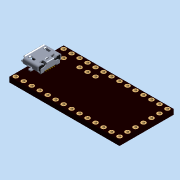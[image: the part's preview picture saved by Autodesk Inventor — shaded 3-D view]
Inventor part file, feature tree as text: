
AUTODESK INVENTOR PART (.ipt)
format: ipt  version: 2015 (Build 190159000, 159)  size: 808,960 bytes
history: native  units: mm (DEFAULTED — no unit token found)
features: hole x37, other x3
ambient origin geometry x8: Origin, YZ Plane, XZ Plane, XY Plane, X Axis, Y Axis, Z Axis, Center Point
bodies: Solid1 (feature_tree)
feature tree (40):
  other  "Teensy 3.1.iam"
  other  "Teensy 3.1 PCB.ipt:1"
  other  "micro_usb_47346-0001.ipt:1"
  hole  "Hole metalization.ipt:1"  [1 undecoded]
  hole  "Hole metalization.ipt:2"  [1 undecoded]
  hole  "Hole metalization.ipt:3"  [1 undecoded]
  hole  "Hole metalization.ipt:4"  [1 undecoded]
  hole  "Hole metalization.ipt:5"  [1 undecoded]
  hole  "Hole metalization.ipt:6"  [1 undecoded]
  hole  "Hole metalization.ipt:7"  [1 undecoded]
  hole  "Hole metalization.ipt:8"  [1 undecoded]
  hole  "Hole metalization.ipt:9"  [1 undecoded]
  hole  "Hole metalization.ipt:10"  [1 undecoded]
  hole  "Hole metalization.ipt:11"  [1 undecoded]
  hole  "Hole metalization.ipt:12"  [1 undecoded]
  hole  "Hole metalization.ipt:13"  [1 undecoded]
  hole  "Hole metalization.ipt:14"  [1 undecoded]
  hole  "Hole metalization.ipt:15"  [1 undecoded]
  hole  "Hole metalization.ipt:16"  [1 undecoded]
  hole  "Hole metalization.ipt:17"  [1 undecoded]
  hole  "Hole metalization.ipt:18"  [1 undecoded]
  hole  "Hole metalization.ipt:19"  [1 undecoded]
  hole  "Hole metalization.ipt:20"  [1 undecoded]
  hole  "Hole metalization.ipt:21"  [1 undecoded]
  hole  "Hole metalization.ipt:22"  [1 undecoded]
  hole  "Hole metalization.ipt:23"  [1 undecoded]
  hole  "Hole metalization.ipt:24"  [1 undecoded]
  hole  "Hole metalization.ipt:25"  [1 undecoded]
  hole  "Hole metalization.ipt:26"  [1 undecoded]
  hole  "Hole metalization.ipt:27"  [1 undecoded]
  hole  "Hole metalization.ipt:28"  [1 undecoded]
  hole  "Hole metalization.ipt:29"  [1 undecoded]
  hole  "Hole metalization.ipt:30"  [1 undecoded]
  hole  "Hole metalization.ipt:31"  [1 undecoded]
  hole  "Hole metalization.ipt:32"  [1 undecoded]
  hole  "Hole metalization.ipt:33"  [1 undecoded]
  hole  "Hole metalization.ipt:34"  [1 undecoded]
  hole  "Hole metalization.ipt:35"  [1 undecoded]
  hole  "Hole metalization.ipt:36"  [1 undecoded]
  hole  "Hole metalization.ipt:37"  [1 undecoded]
note: 37 required parameter values undecoded (feature->parameter linkage not recoverable at this tier; creation-order binding heuristic only, values carry confidence <= 0.55)
